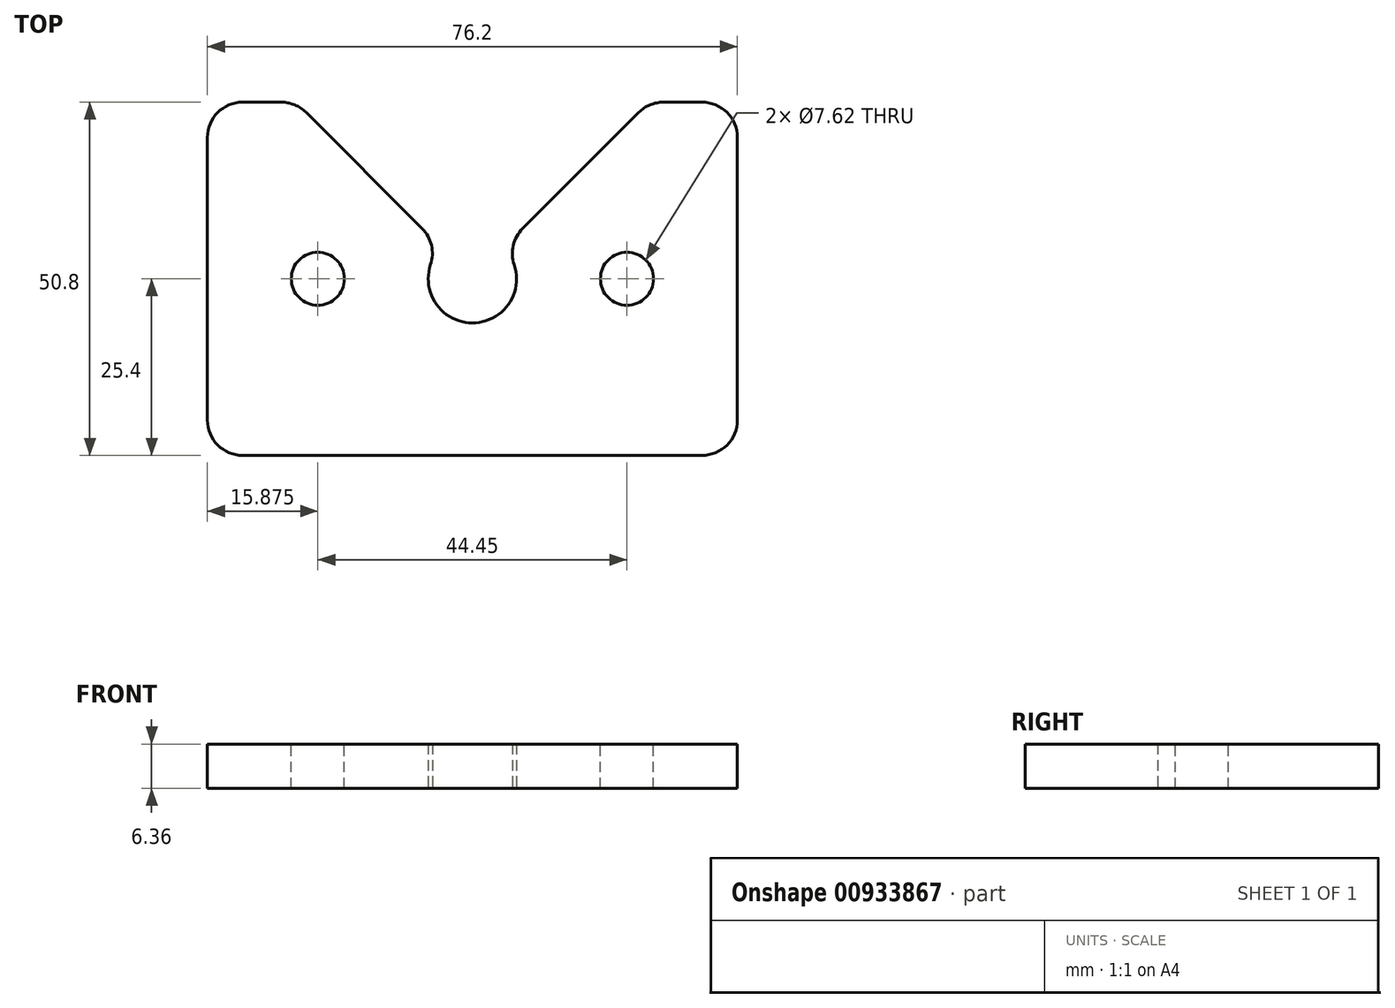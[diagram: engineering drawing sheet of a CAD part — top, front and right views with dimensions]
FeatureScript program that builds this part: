
annotation { "Feature Type Name" : "Feature", "Feature Type Description" : "" }
export const myFeature = defineFeature(function(context is Context, id is Id, definition is map)
    precondition{}
    {
        {
            var Q0;
            Q0=qCreatedBy(makeId("Top.planeOp"),FACE);
            var sketch = newSketch(context, id + "F0", { "sketchPlane" : qUnion([Q0])});
            skLineSegment(sketch, "E0.bottom", {"start": v(38.1, -25.4) * mm, "end": v(-38.1, -25.4) * mm});
            skLineSegment(sketch, "E0.top", {"start": v(38.1, 25.4) * mm, "end": v(25.4, 25.4) * mm});
            skLineSegment(sketch, "E0.left", {"start": v(38.1, -25.4) * mm, "end": v(38.1, 25.4) * mm});
            skLineSegment(sketch, "E0.right", {"start": v(-38.1, -25.4) * mm, "end": v(-38.1, 25.4) * mm});
            skPoint(sketch, "E0.middle", {"position": v(0, 0) * mm});
            skLineSegment(sketch, "E1", {"start": v(-25.4, 25.4) * mm, "end": v(-4.5, 4.5) * mm});
            skLineSegment(sketch, "E2", {"start": v(25.4, 25.4) * mm, "end": v(4.5, 4.5) * mm});
            skLineSegment(sketch, "E3.trimOffspring", {"start": v(-25.4, 25.4) * mm, "end": v(-38.1, 25.4) * mm});
            skArc(sketch, "E4", {"start": v(-4.5, 4.5) * mm, "mid": v(0, -6.35) * mm, "end": v(4.5, 4.5) * mm});
            skSolve(sketch);
        }
        {
            var Q0;
            Q0 = qSketchRegion(id + "F0", true);
            extrude(context, id + "F1", {"entities" : qUnion([Q0]), "depth" : 6.35 * mm, "offsetDistance" : 25.4 * mm, "symmetric" : true});
        }
        {
            var Q0;
            Q0=makeQuery(id+"F1.opExtrude","SWEPT_EDGE",EDGE,{"disambiguationData":[OSD([sQuery(id+"F0.wireOp",EDGE,"E2"),sQuery(id+"F0.wireOp",EDGE,"E4")])]});
            var Q1;
            Q1=makeQuery(id+"F1.opExtrude","SWEPT_EDGE",EDGE,{"disambiguationData":[OSD([sQuery(id+"F0.wireOp",EDGE,"E1"),sQuery(id+"F0.wireOp",EDGE,"E4")])]});
            var Q2;
            Q2=makeQuery(id+"F1.opExtrude","SWEPT_EDGE",EDGE,{"disambiguationData":[OSD([sQuery(id+"F0.wireOp",EDGE,"E1"),sQuery(id+"F0.wireOp",EDGE,"E3.trimOffspring")])]});
            var Q3;
            Q3=makeQuery(id+"F1.opExtrude","SWEPT_EDGE",EDGE,{"disambiguationData":[OSD([sQuery(id+"F0.wireOp",EDGE,"E0.right"),sQuery(id+"F0.wireOp",EDGE,"E3.trimOffspring")])]});
            var Q4;
            Q4=makeQuery(id+"F1.opExtrude","SWEPT_EDGE",EDGE,{"disambiguationData":[OSD([sQuery(id+"F0.wireOp",EDGE,"E0.bottom"),sQuery(id+"F0.wireOp",EDGE,"E0.right")])]});
            var Q5;
            Q5=makeQuery(id+"F1.opExtrude","SWEPT_EDGE",EDGE,{"disambiguationData":[OSD([sQuery(id+"F0.wireOp",EDGE,"E0.top"),sQuery(id+"F0.wireOp",EDGE,"E0.left")])]});
            var Q6;
            Q6=makeQuery(id+"F1.opExtrude","SWEPT_EDGE",EDGE,{"disambiguationData":[OSD([sQuery(id+"F0.wireOp",EDGE,"E0.top"),sQuery(id+"F0.wireOp",EDGE,"E2")])]});
            var Q7;
            Q7=makeQuery(id+"F1.opExtrude","SWEPT_EDGE",EDGE,{"disambiguationData":[OSD([sQuery(id+"F0.wireOp",EDGE,"E0.bottom"),sQuery(id+"F0.wireOp",EDGE,"E0.left")])]});
            fillet(context, id + "F2", {"entities" : qUnion([Q0, Q1, Q2, Q3, Q4, Q5, Q6, Q7]), "radius" : 5.08 * mm, "tangentPropagation" : true, "allowEdgeOverflow" : false});
        }
        {
            var Q0;
            Q0=makeQuery(id+"F1.opExtrude","CAP_FACE",FACE,{"disambiguationData":[OSD([sQuery(id+"F0.wireOp",EDGE,"E0.bottom"),sQuery(id+"F0.wireOp",EDGE,"E0.top"),sQuery(id+"F0.wireOp",EDGE,"E0.left"),sQuery(id+"F0.wireOp",EDGE,"E0.right"),sQuery(id+"F0.wireOp",EDGE,"E1"),sQuery(id+"F0.wireOp",EDGE,"E2"),sQuery(id+"F0.wireOp",EDGE,"E3.trimOffspring"),sQuery(id+"F0.wireOp",EDGE,"E4")])],"isStart":false});
            var sketch = newSketch(context, id + "F3", { "sketchPlane" : qUnion([Q0])});
            skCircle(sketch, "E5", {"center": v(-22.22, 0) * mm, "radius": 3.81 * mm});
            skCircle(sketch, "E6", {"center": v(22.22, 0) * mm, "radius": 3.81 * mm});
            skLineSegment(sketch, "E7", {"start": v(-22.22, 0) * mm, "end": v(-38.1, 0) * mm});
            skLineSegment(sketch, "E8", {"start": v(22.22, 0) * mm, "end": v(38.1, 0) * mm});
            skSolve(sketch);
        }
        {
            var Q0;
            Q0 = qSketchRegion(id + "F3", true);
            extrude(context, id + "F4", {"entities" : qUnion([Q0]), "operationType" : NewBodyOperationType.REMOVE, "oppositeDirection" : true, "depth" : 25.4 * mm, "offsetDistance" : 25.4 * mm});
        }
    });
